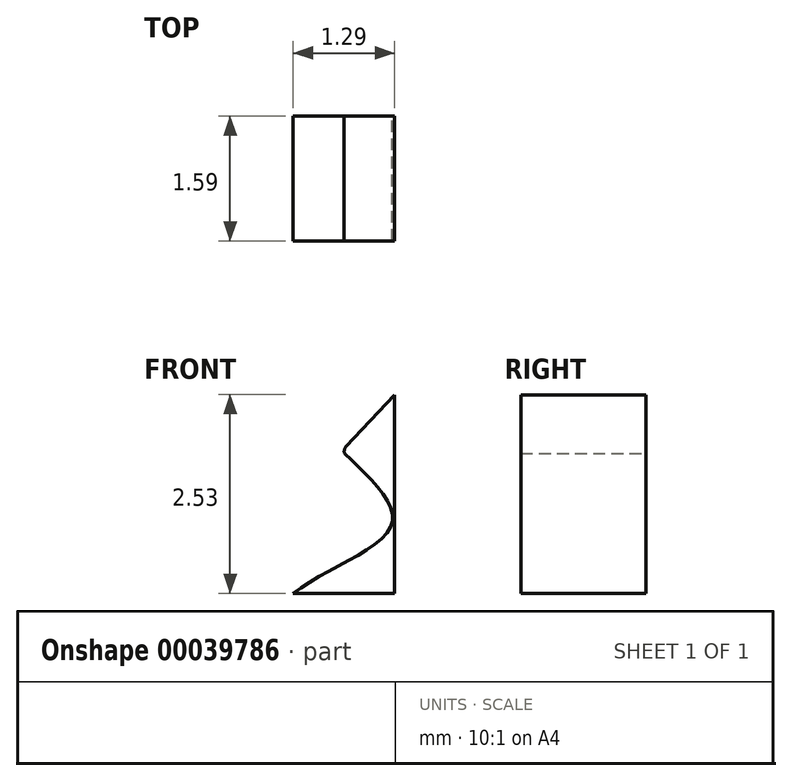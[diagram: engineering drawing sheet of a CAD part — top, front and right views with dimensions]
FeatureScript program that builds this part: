
annotation { "Feature Type Name" : "Feature", "Feature Type Description" : "" }
export const myFeature = defineFeature(function(context is Context, id is Id, definition is map)
    precondition{}
    {
        {
            var Q0;
            Q0=qCreatedBy(makeId("Front.planeOp"),FACE);
            var sketch = newSketch(context, id + "F0", { "sketchPlane" : qUnion([Q0])});
            skLineSegment(sketch, "E0", {"start": v(0, 0) * mm, "end": v(0, 1.78) * mm});
            skLineSegment(sketch, "E1", {"start": v(0, 0) * mm, "end": v(0, 0.89) * mm, "construction": true});
            skLineSegment(sketch, "E2", {"start": v(0, 0.89) * mm, "end": v(0, 0.88) * mm, "construction": true});
            skLineSegment(sketch, "E3", {"start": v(0, 2.53) * mm, "end": v(0, 1.78) * mm});
            skLineSegment(sketch, "E4", {"start": v(0, 2.53) * mm, "end": v(-0.62, 1.87) * mm});
            skArc(sketch, "E5", {"start": v(-0.62, 1.87) * mm, "mid": v(-0.64, 1.83) * mm, "end": v(-0.64, 1.78) * mm});
            skLineSegment(sketch, "E6", {"start": v(0, 0) * mm, "end": v(-1.29, 0) * mm});
            skFitSpline(sketch, "E7", {"points": [v(-0.64, 1.78) * mm, v(-0.04, 0.89) * mm, v(-1.29, 0) * mm], "startDerivative": vector(1.87, -1.82) * mm, "endDerivative": vector(-2.1, -1.73) * mm});
            skSolve(sketch);
        }
        {
            var Q0;
            Q0 = qSketchRegion(id + "F0", true);
            extrude(context, id + "F1", {"entities" : qUnion([Q0]), "depth" : 1.59 * mm});
        }
    });
